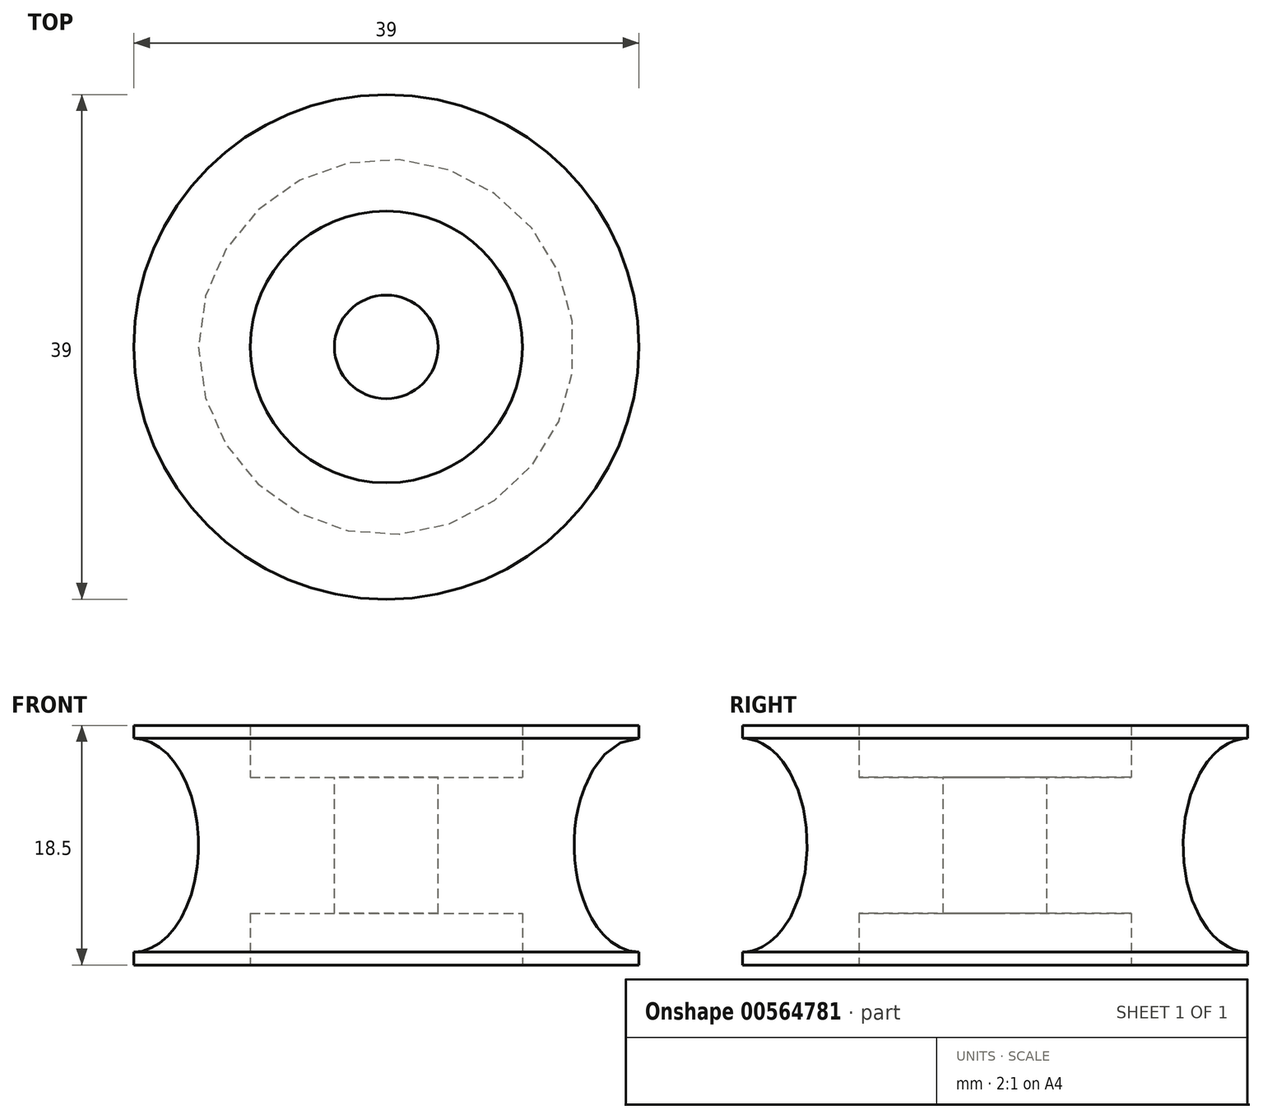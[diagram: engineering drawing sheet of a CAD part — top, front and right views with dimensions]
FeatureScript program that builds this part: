
annotation { "Feature Type Name" : "Feature", "Feature Type Description" : "" }
export const myFeature = defineFeature(function(context is Context, id is Id, definition is map)
    precondition{}
    {
        {
            var Q0;
            Q0=qCreatedBy(makeId("Front.planeOp"),FACE);
            var sketch = newSketch(context, id + "F0", { "sketchPlane" : qUnion([Q0])});
            skLineSegment(sketch, "E0", {"start": v(10.5, 9.25) * mm, "end": v(19.5, 9.25) * mm});
            skLineSegment(sketch, "E1", {"start": v(19.5, 9.25) * mm, "end": v(19.5, 8.25) * mm});
            skLineSegment(sketch, "E2", {"start": v(19.5, -9.25) * mm, "end": v(19.5, -8.25) * mm});
            skLineSegment(sketch, "E3", {"start": v(0, 0) * mm, "end": v(0, 5.25) * mm});
            skLineSegment(sketch, "E4", {"start": v(0, 5.25) * mm, "end": v(10.5, 5.25) * mm});
            skLineSegment(sketch, "E5", {"start": v(10.5, 5.25) * mm, "end": v(10.5, 9.25) * mm});
            skLineSegment(sketch, "E6", {"start": v(19.5, -9.25) * mm, "end": v(10.5, -9.25) * mm});
            skLineSegment(sketch, "E7", {"start": v(10.5, -9.25) * mm, "end": v(10.5, -5.25) * mm});
            skLineSegment(sketch, "E8", {"start": v(10.5, -5.25) * mm, "end": v(0, -5.25) * mm});
            skLineSegment(sketch, "E9", {"start": v(0, -5.25) * mm, "end": v(0, 0) * mm});
            skEllipticalArc(sketch, "E10", {});
            const initialGuessF0  = {"E10": [0.0195, 0, 0, 1, 0.00825, 0.005, 0, 3.141592653589793]};
            skSetInitialGuess(sketch, initialGuessF0);
            skSolve(sketch);
        }
        {
            var Q0;
            Q0=makeQuery(id+"F0.imprint","IMPRINT",FACE,{"disambiguationData":[TD([[makeQuery(id+"F0.imprint","IMPRINT",EDGE,{"derivedFrom":sQuery(id+"F0.wireOp",EDGE,"E0")}),-1.0]])]});
            var Q1;
            Q1=sQuery(id+"F0.wireOp",EDGE,"E3");
            revolve(context, id + "F1", {"entities" : qUnion([Q0]), "axis" : qUnion([Q1]), "revolveType" : RevolveType.FULL});
        }
        {
            var Q0;
            Q0=makeQuery(id+"F1.opRevolve","SWEPT_FACE",FACE,{"disambiguationData":[OSD([sQuery(id+"F0.wireOp",EDGE,"E4")])]});
            var sketch = newSketch(context, id + "F2", { "sketchPlane" : qUnion([Q0])});
            skCircle(sketch, "E11", {"center": v(0, 0) * mm, "radius": 4 * mm});
            skSolve(sketch);
        }
        {
            var Q0;
            Q0=qSketchRegion(id+"F2",true);
            extrude(context, id + "F3", {"entities" : qUnion([Q0]), "operationType" : NewBodyOperationType.REMOVE, "endBound" : BoundingType.THROUGH_ALL, "oppositeDirection" : true, "depth" : 25 * mm, "offsetDistance" : 25 * mm});
        }
    });
